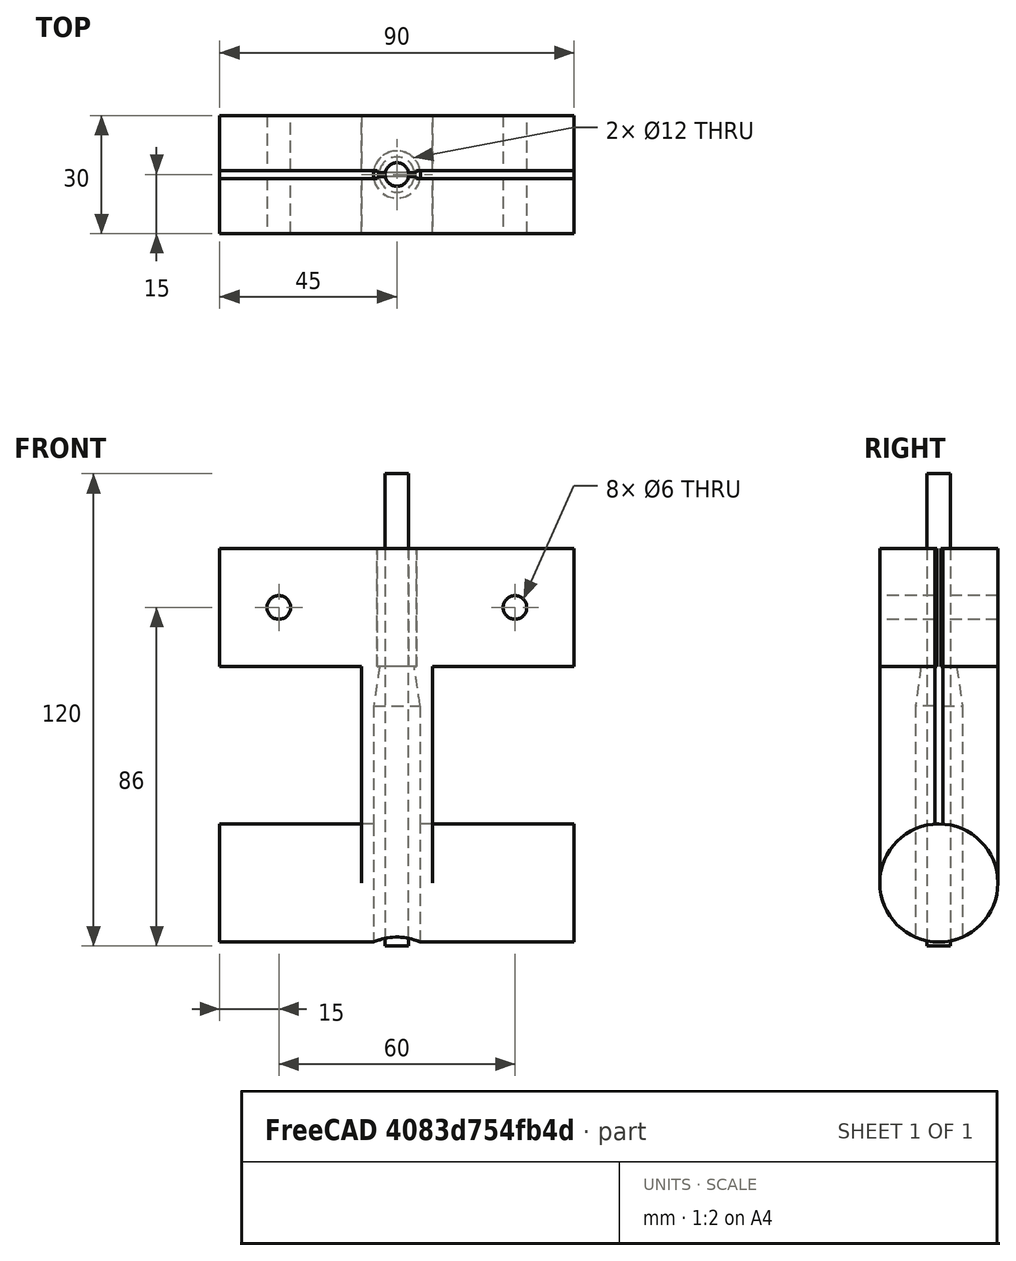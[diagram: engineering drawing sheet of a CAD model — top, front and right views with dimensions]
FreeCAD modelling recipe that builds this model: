
FCSTD DOCUMENT  (FreeCAD 0.20R29410 (Git))
Label: drill
License: All rights reserved
LicenseURL: http://en.wikipedia.org/wiki/All_rights_reserved
objects: Part::Cut×17, Part::Box×12, Part::Cylinder×10, Part::MultiFuse×4, Part::Cone×2
note: 45 computed .brp shape members not serialized (recipe doc carries the construction recipe); baked Part::Feature solids carry a one-line shape summary decoded from their .brp

FEATURE [Part::Box] Box  label="Cube"
  AttacherType = Attacher::AttachEngine3D
  Height = 30
  Length = 90
  Width = 30
FEATURE [Part::Cylinder] Cylinder
  Angle = 360
  AttacherType = Attacher::AttachEngine3D
  FirstAngle = 0
  Height = 40
  Placement = pos=(15,-3,15) rot=(-1,0,0;1.5708rad)
  Radius = 3
  SecondAngle = 0
FEATURE [Part::Cylinder] Cylinder001
  Angle = 360
  AttacherType = Attacher::AttachEngine3D
  FirstAngle = 0
  Height = 120
  Placement = pos=(45,15,-71) rot=(0,0,1;0rad)
  Radius = 3
  SecondAngle = 0
FEATURE [Part::Cylinder] Cylinder002
  Angle = 360
  AttacherType = Attacher::AttachEngine3D
  FirstAngle = 0
  Height = 40
  Placement = pos=(75,-3,15) rot=(1,0,0;4.71239rad)
  Radius = 3
  SecondAngle = 0
FEATURE [Part::Cylinder] Cylinder004
  Angle = 360
  AttacherType = Attacher::AttachEngine3D
  FirstAngle = 0
  Height = 90
  Placement = pos=(1.05e-14,15,-55) rot=(0.57735,-0.57735,0.57735;4.18879rad)
  Radius = 15
  SecondAngle = 0
FEATURE [Part::Cylinder] Cylinder005
  Angle = 360
  AttacherType = Attacher::AttachEngine3D
  FirstAngle = 0
  Height = 120
  Placement = pos=(45,15,-130) rot=(0,0,1;0rad)
  Radius = 6
  SecondAngle = 0
FEATURE [Part::Cone] Cone
  Angle = 360
  AttacherType = Attacher::AttachEngine3D
  Height = 20
  Placement = pos=(45,15,10) rot=(0,1,0;3.14159rad)
  Radius1 = 3
  Radius2 = 6
FEATURE [Part::Box] Box001  label="Cube001"
  AttacherType = Attacher::AttachEngine3D
  Height = 65
  Length = 18
  Placement = pos=(36,0,-55) rot=(0,0,1;0rad)
  Width = 30
FEATURE [Part::Box] Box002  label="Cube002"
  AttacherType = Attacher::AttachEngine3D
  Height = 120
  Length = 90
  Placement = pos=(0,14.5,-88) rot=(0,0,1;0rad)
  Width = 1
FEATURE [Part::Box] Box003  label="Cube003"
  AttacherType = Attacher::AttachEngine3D
  Height = 120
  Length = 90
  Placement = pos=(50,14,-88) rot=(0,0,1;0rad)
  Width = 2
FEATURE [Part::Cut] Cut
  Base = -> Box
  Tool = -> Box002
FEATURE [Part::Box] Box004  label="Cube004"
  AttacherType = Attacher::AttachEngine3D
  Height = 120
  Length = 90
  Placement = pos=(-50,14,-88) rot=(0,0,1;0rad)
  Width = 2
FEATURE [Part::Box] Box005  label="Cube005"
  AttacherType = Attacher::AttachEngine3D
  Height = 120
  Length = 90
  Placement = pos=(0,14,-88) rot=(0,0,1;0rad)
  Width = 2
FEATURE [Part::Cut] Cut001
  Base = -> Cut
  Tool = -> Box004
FEATURE [Part::Cut] Cut002
  Base = -> Cut001
  Tool = -> Box003
FEATURE [Part::Cut] Cut003
  Base = -> Box001
  Tool = -> Box005
FEATURE [Part::MultiFuse] Fusion
  Shapes = -> [Cut003,Cylinder004]
FEATURE [Part::Cut] Cut004
  Base = -> Fusion
  Tool = -> Cylinder005
FEATURE [Part::Cut] Cut005
  Base = -> Cut004
  Tool = -> Cone
FEATURE [Part::Cut] Cut006
  Base = -> Cut002
  Tool = -> Cylinder002
FEATURE [Part::Cut] Cut007
  Base = -> Cut006
  Tool = -> Cylinder
FEATURE [Part::MultiFuse] Fusion001
  Shapes = -> [Cut005,Cut007]
FEATURE [Part::Box] Box006  label="Cube006"
  AttacherType = Attacher::AttachEngine3D
  Height = 30
  Length = 90
  Width = 30
FEATURE [Part::Box] Box007  label="Cube007"
  AttacherType = Attacher::AttachEngine3D
  Height = 65
  Length = 18
  Placement = pos=(36,0,-55) rot=(0,0,1;0rad)
  Width = 30
FEATURE [Part::Box] Box008  label="Cube008"
  AttacherType = Attacher::AttachEngine3D
  Height = 120
  Length = 90
  Placement = pos=(0,14.5,-88) rot=(0,0,1;0rad)
  Width = 1
FEATURE [Part::Box] Box009  label="Cube009"
  AttacherType = Attacher::AttachEngine3D
  Height = 120
  Length = 90
  Placement = pos=(50,14,-88) rot=(0,0,1;0rad)
  Width = 2
FEATURE [Part::Box] Box010  label="Cube010"
  AttacherType = Attacher::AttachEngine3D
  Height = 120
  Length = 90
  Placement = pos=(-50,14,-88) rot=(0,0,1;0rad)
  Width = 2
FEATURE [Part::Box] Box011  label="Cube011"
  AttacherType = Attacher::AttachEngine3D
  Height = 120
  Length = 90
  Placement = pos=(0,14,-88) rot=(0,0,1;0rad)
  Width = 2
FEATURE [Part::Cone] Cone001
  Angle = 360
  AttacherType = Attacher::AttachEngine3D
  Height = 20
  Placement = pos=(45,15,10) rot=(0,1,0;3.14159rad)
  Radius1 = 3
  Radius2 = 6
FEATURE [Part::Cut] Cut009
  Base = -> Box006
  Tool = -> Box008
FEATURE [Part::Cut] Cut010
  Base = -> Cut009
  Tool = -> Box010
FEATURE [Part::Cut] Cut011
  Base = -> Cut010
  Tool = -> Box009
FEATURE [Part::Cut] Cut012
  Base = -> Box007
  Tool = -> Box011
FEATURE [Part::Cylinder] Cylinder006
  Angle = 360
  AttacherType = Attacher::AttachEngine3D
  FirstAngle = 0
  Height = 40
  Placement = pos=(15,-3,15) rot=(-1,0,0;1.5708rad)
  Radius = 3
  SecondAngle = 0
FEATURE [Part::Cylinder] Cylinder007
  Angle = 360
  AttacherType = Attacher::AttachEngine3D
  FirstAngle = 0
  Height = 120
  Placement = pos=(45,15,-71) rot=(0,0,1;0rad)
  Radius = 3
  SecondAngle = 0
FEATURE [Part::Cylinder] Cylinder008
  Angle = 360
  AttacherType = Attacher::AttachEngine3D
  FirstAngle = 0
  Height = 40
  Placement = pos=(75,-3,15) rot=(-1,0,0;1.5708rad)
  Radius = 3
  SecondAngle = 0
FEATURE [Part::Cut] Cut015
  Base = -> Cut011
  Tool = -> Cylinder008
FEATURE [Part::Cut] Cut016
  Base = -> Cut015
  Tool = -> Cylinder006
FEATURE [Part::Cylinder] Cylinder009
  Angle = 360
  AttacherType = Attacher::AttachEngine3D
  FirstAngle = 0
  Height = 90
  Placement = pos=(1.1e-14,15,-55) rot=(0.57735,-0.57735,0.57735;4.18879rad)
  Radius = 15
  SecondAngle = 0
FEATURE [Part::Cylinder] Cylinder010
  Angle = 360
  AttacherType = Attacher::AttachEngine3D
  FirstAngle = 0
  Height = 120
  Placement = pos=(45,15,-130) rot=(0,0,1;0rad)
  Radius = 6
  SecondAngle = 0
FEATURE [Part::MultiFuse] Fusion002
  Shapes = -> [Cut012,Cylinder009]
FEATURE [Part::Cut] Cut013
  Base = -> Fusion002
  Tool = -> Cylinder010
FEATURE [Part::Cut] Cut014
  Base = -> Cut013
  Tool = -> Cone001
FEATURE [Part::MultiFuse] Fusion003
  Shapes = -> [Cut014,Cut016]
FEATURE [Part::Cut] Cut017  label="Deill_6"
  Base = -> Fusion003
  Tool = -> Cylinder007
